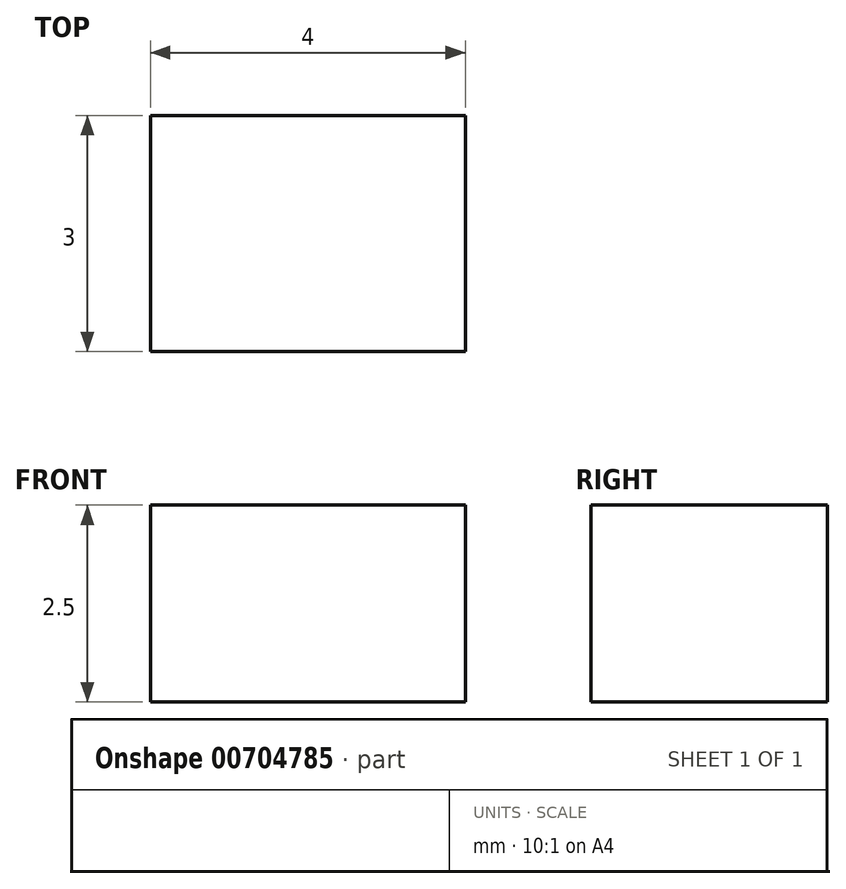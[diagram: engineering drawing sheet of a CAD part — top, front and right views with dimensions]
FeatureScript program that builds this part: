
annotation { "Feature Type Name" : "Feature", "Feature Type Description" : "" }
export const myFeature = defineFeature(function(context is Context, id is Id, definition is map)
    precondition{}
    {
        {
            var Q0;
            Q0=qCreatedBy(makeId("Top.planeOp"),FACE);
            var sketch = newSketch(context, id + "F0", { "sketchPlane" : qUnion([Q0])});
            skLineSegment(sketch, "E0.bottom", {"start": v(2, -1.5) * mm, "end": v(-2, -1.5) * mm});
            skLineSegment(sketch, "E0.top", {"start": v(2, 1.5) * mm, "end": v(-2, 1.5) * mm});
            skLineSegment(sketch, "E0.left", {"start": v(2, -1.5) * mm, "end": v(2, 1.5) * mm});
            skLineSegment(sketch, "E0.right", {"start": v(-2, -1.5) * mm, "end": v(-2, 1.5) * mm});
            skPoint(sketch, "E0.middle", {"position": v(0, 0) * mm});
            skSolve(sketch);
        }
        {
            var Q0;
            Q0 = qSketchRegion(id + "F0", true);
            extrude(context, id + "F1", {"entities" : qUnion([Q0]), "depth" : 2.5 * mm, "offsetDistance" : 25 * mm});
        }
    });
